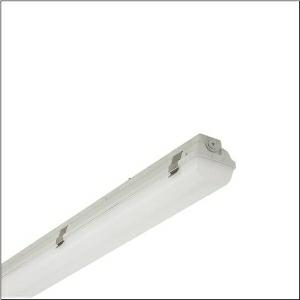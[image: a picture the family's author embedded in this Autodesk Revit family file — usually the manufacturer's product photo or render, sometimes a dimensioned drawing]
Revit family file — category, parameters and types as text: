
# Revit family: monsun_r__21_eco_51fj10mp47a_2b6f
name_source: partatom
category: Lighting Fixtures
units: mm (PartAtom-declared; Revit-internal decimal feet)

## family parameters
Cut with Voids When Loaded = No
Host = Face
Light Source = No
Part Type = Normal
Room Calculation Point = No
Round Connector Dimension = Use Diameter
Shared = No

## types (1)
- --- (1 x LED, 7000 lm, 50 W, 4000K)
    Apparent Load = 50 VA
    CIE Flux Codes = 41 70 89 90 100
    Color Rendering = 80
    Color Temperature = 4000K
    Default Elevation = 1800 mm
    Description = Monsun® 21 Eco, damp-proof luminaire, primary optical cover: diffuser, of PMMA, frosted, light emission: direct distribution, primary light characteristic: symmetric, installation type: suspended mounting, surface-mounted, LED, rated luminous flux: 7.000lm, luminous efficacy: 140lm/W, light colour: 840, colour temperature: 4000K, control gear: ECG Multilumen, with terminal, 3-pole, max. 2.5mm², mains connection: 220..240V, AC, 50/60Hz, rated input power: 50W, housing, of glass-fibre reinforced polyester, light grey (RAL 7035), length: 1.577mm, width: 90mm, height: 95mm, clip for enclosure, of spring steel V2A, protection rating (complete): IP66, insulation class (complete): insulation class I (protective earthing), certification: CE, UKCA, protection symbol: D, impact resistance: IK02, permissible operating ambient temperature: -20..+35°C, corresponds to IFS (International Featured Standards) requirements for safety and quality in the food industry, packaging unit: 1 piece
    Height = 103 mm
    Lamp = 1 x LED
    Lamp Light Flux = 7000 lm
    Lamp Power = 50 W
    Lamp count = 1
    Length = 1577 mm
    Luminous efficacy = 140 lm/W
    Manufacturer = Siteco
    ModVariant = No
    Model = 51FJ10MP47A
    Mounting Place = Ceiling
    Mounting Type = Surface mounted
    Number of Poles = 1
    OnlyDefault = Yes
    Power Factor = 1
    Product Name = Monsun® 21 Eco
    Product group = damp-proof luminaire | ceiling mounted
    ProductGroupID = 300
    Protection Class = Protection class I
    Protection Degree = IP 66
    RLX_Detail_Level = 1
    RlxData = <blob elided: 33897 chars, md5=c53898ca>
    Socket = socket
    Standby Power = 0 W
    System Light Flux = 7000 lm
    System Power = 50 W
    Type Comments = factory setting: luminous flux: 100 % | (ON | ON | ON | ON) | 350 mA
    Type Image = l_1007218.jpg
    URL = http://relux.com
    VarID = @adj_055469
    Voltage = 0 V
    Weight = 0.00 kg
    Width = 90 mm

## geometry (parser evidence)
native form markers: Blend x4, Sweep x14
no freeform markers — native parametric forms only
